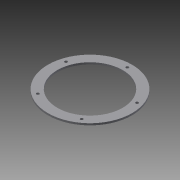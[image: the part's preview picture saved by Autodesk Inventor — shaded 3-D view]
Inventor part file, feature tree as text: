
AUTODESK INVENTOR PART (.ipt)
format: ipt  version: 2015 (Build 190159000, 159)  size: 97,280 bytes
history: native  units: in
note: dims shown in document units (in); Inventor stores cm internally (conversion verified against a paired STEP export)
features: extrude x2, sketch x2
ambient origin geometry x8: Origin, YZ Plane, XZ Plane, XY Plane, X Axis, Y Axis, Z Axis, Center Point
bodies: Solid1 (feature_tree)
feature tree (4):
  extrude  "Extrusion1"  Depth=0.3937in
  extrude  "Extrusion2"  Depth=0.0787in
  sketch  "Sketch1"  dims[d0=0.3937in d1=2.7559in]
  sketch  "Sketch2"  dims[d2=0.0787in d3=0.0in d4=0.1181in d5=1.5748in d6=1.9685in d8=360.0deg d10=0.1181in d11=0.0in]
